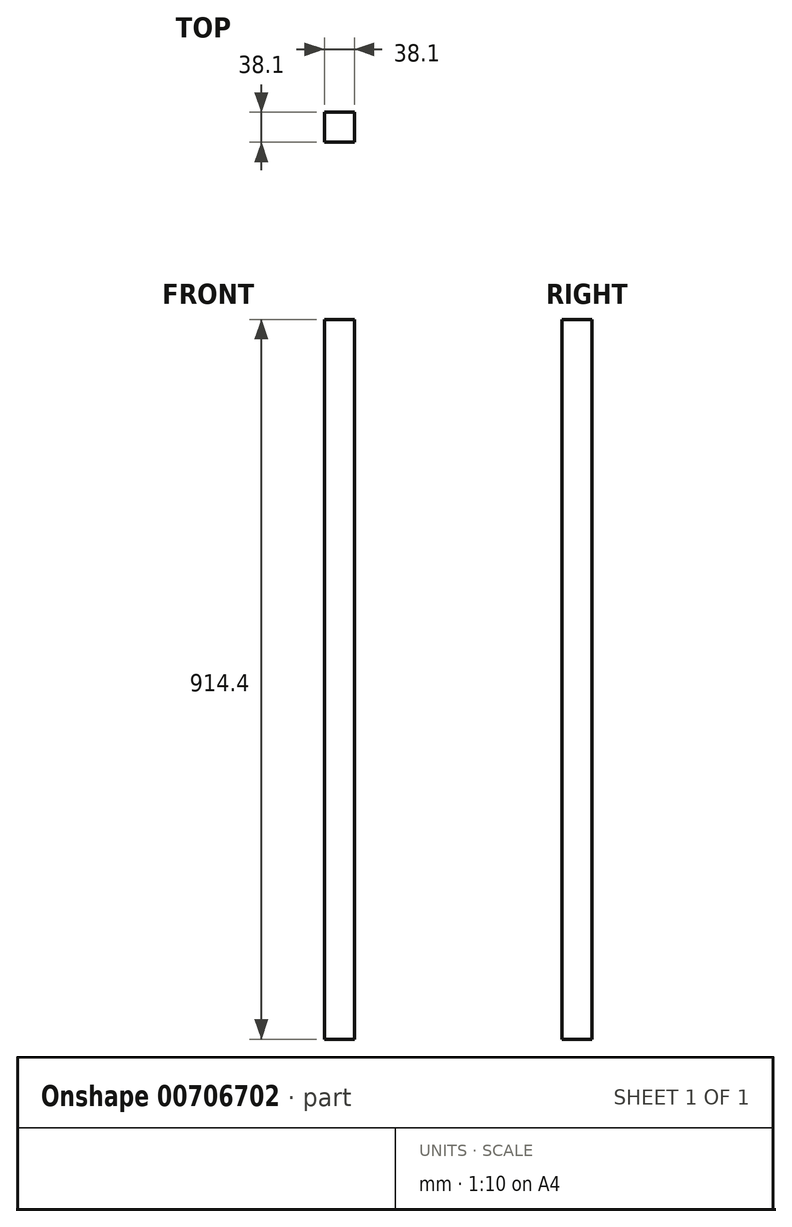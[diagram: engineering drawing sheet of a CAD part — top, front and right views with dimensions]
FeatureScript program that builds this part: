
annotation { "Feature Type Name" : "Feature", "Feature Type Description" : "" }
export const myFeature = defineFeature(function(context is Context, id is Id, definition is map)
    precondition{}
    {
        {
            var Q0;
            Q0=qCreatedBy(makeId("Right.planeOp"),FACE);
            var sketch = newSketch(context, id + "F0", { "sketchPlane" : qUnion([Q0])});
            skLineSegment(sketch, "E0.bottom", {"start": v(0, 0) * mm, "end": v(38.1, 0) * mm});
            skLineSegment(sketch, "E0.top", {"start": v(0, 914.4) * mm, "end": v(38.1, 914.4) * mm});
            skLineSegment(sketch, "E0.left", {"start": v(0, 0) * mm, "end": v(0, 914.4) * mm});
            skLineSegment(sketch, "E0.right", {"start": v(38.1, 0) * mm, "end": v(38.1, 914.4) * mm});
            skSolve(sketch);
        }
        {
            var Q0;
            Q0=makeQuery(id+"F0.imprint","IMPRINT",FACE,{"disambiguationData":[TD([[makeQuery(id+"F0.imprint","IMPRINT",EDGE,{"derivedFrom":sQuery(id+"F0.wireOp",EDGE,"E0.bottom")}),1.0]])]});
            extrude(context, id + "F1", {"entities" : qUnion([Q0]), "depth" : 38.1 * mm, "offsetDistance" : 25.4 * mm});
        }
    });
